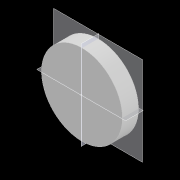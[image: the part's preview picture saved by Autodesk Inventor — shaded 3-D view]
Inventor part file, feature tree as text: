
AUTODESK INVENTOR PART (.ipt)
format: ipt  version: 2020 (Build 240168000, 168)  size: 81,408 bytes
history: native  units: mm
features: other x1, extrude x1, sketch x1
ambient origin geometry x8: Origin, YZ Plane, XZ Plane, XY Plane, X Axis, Y Axis, Z Axis, Center Point
bodies: Body1 (feature_tree)
feature tree (3):
  other  "實體1"
  extrude  "擠出1"  Depth=50.0mm
  sketch  "草圖1"
